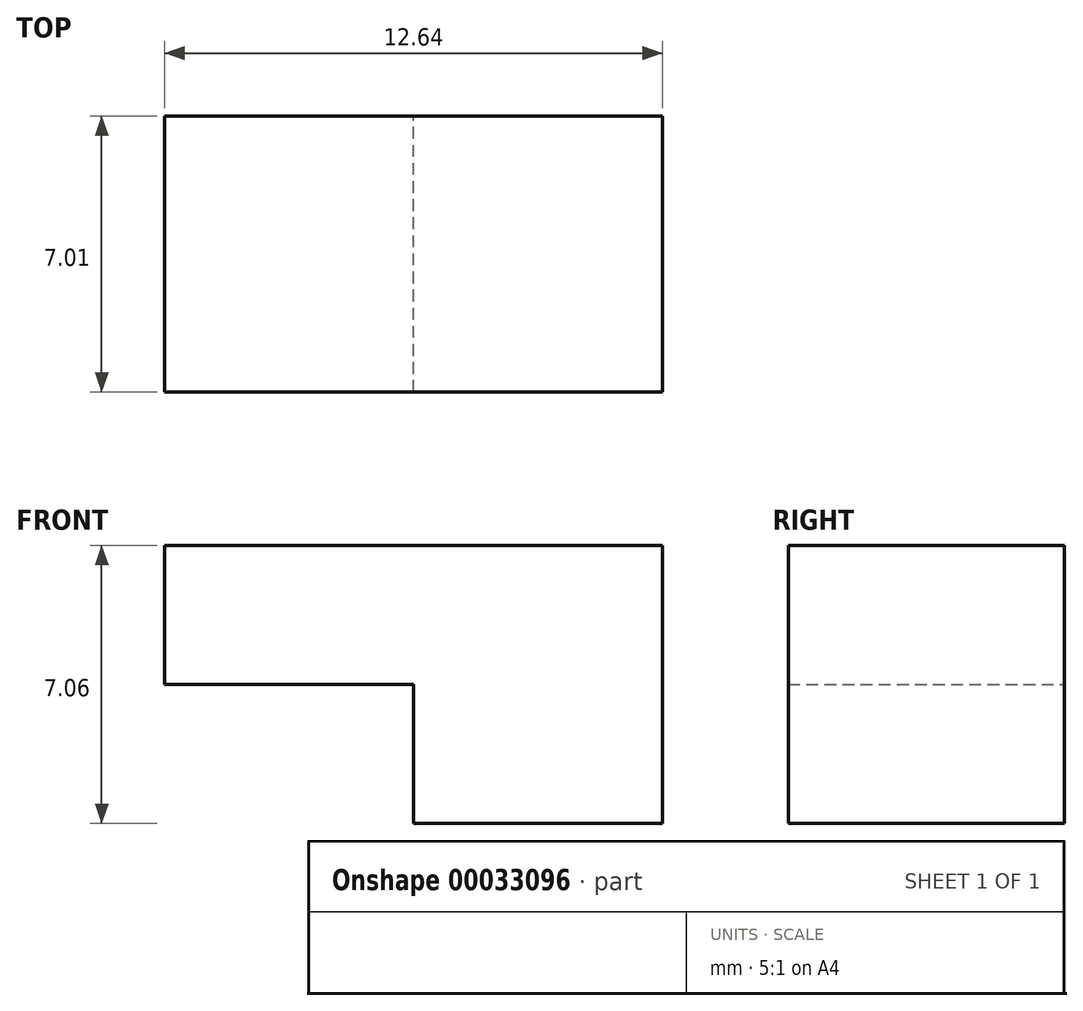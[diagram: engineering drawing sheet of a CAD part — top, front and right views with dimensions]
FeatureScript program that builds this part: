
annotation { "Feature Type Name" : "Feature", "Feature Type Description" : "" }
export const myFeature = defineFeature(function(context is Context, id is Id, definition is map)
    precondition{}
    {
        {
            var Q0;
            Q0=qCreatedBy(makeId("Front.planeOp"),FACE);
            var sketch = newSketch(context, id + "F0", { "sketchPlane" : qUnion([Q0])});
            skLineSegment(sketch, "E0.rect.bottom", {"start": v(6.32, -3.53) * mm, "end": v(0, -3.53) * mm});
            skLineSegment(sketch, "E0.rect.top", {"start": v(6.32, 3.53) * mm, "end": v(-6.32, 3.53) * mm});
            skLineSegment(sketch, "E0.rect.left", {"start": v(6.32, -3.53) * mm, "end": v(6.32, 3.53) * mm});
            skLineSegment(sketch, "E0.rect.right", {"start": v(-6.32, 0) * mm, "end": v(-6.32, 3.53) * mm});
            skPoint(sketch, "E0.rect.middle", {"position": v(0, 0) * mm});
            skLineSegment(sketch, "E1.top", {"start": v(-6.32, 0) * mm, "end": v(0, 0) * mm});
            skLineSegment(sketch, "E1.right", {"start": v(0, -3.53) * mm, "end": v(0, 0) * mm});
            skPoint(sketch, "E2.orphan", {"position": v(-6.32, -3.53) * mm});
            skSolve(sketch);
        }
        {
            var Q0;
            Q0 = qSketchRegion(id + "F0", true);
            extrude(context, id + "F1", {"entities" : qUnion([Q0]), "depth" : 7 * mm});
        }
    });
